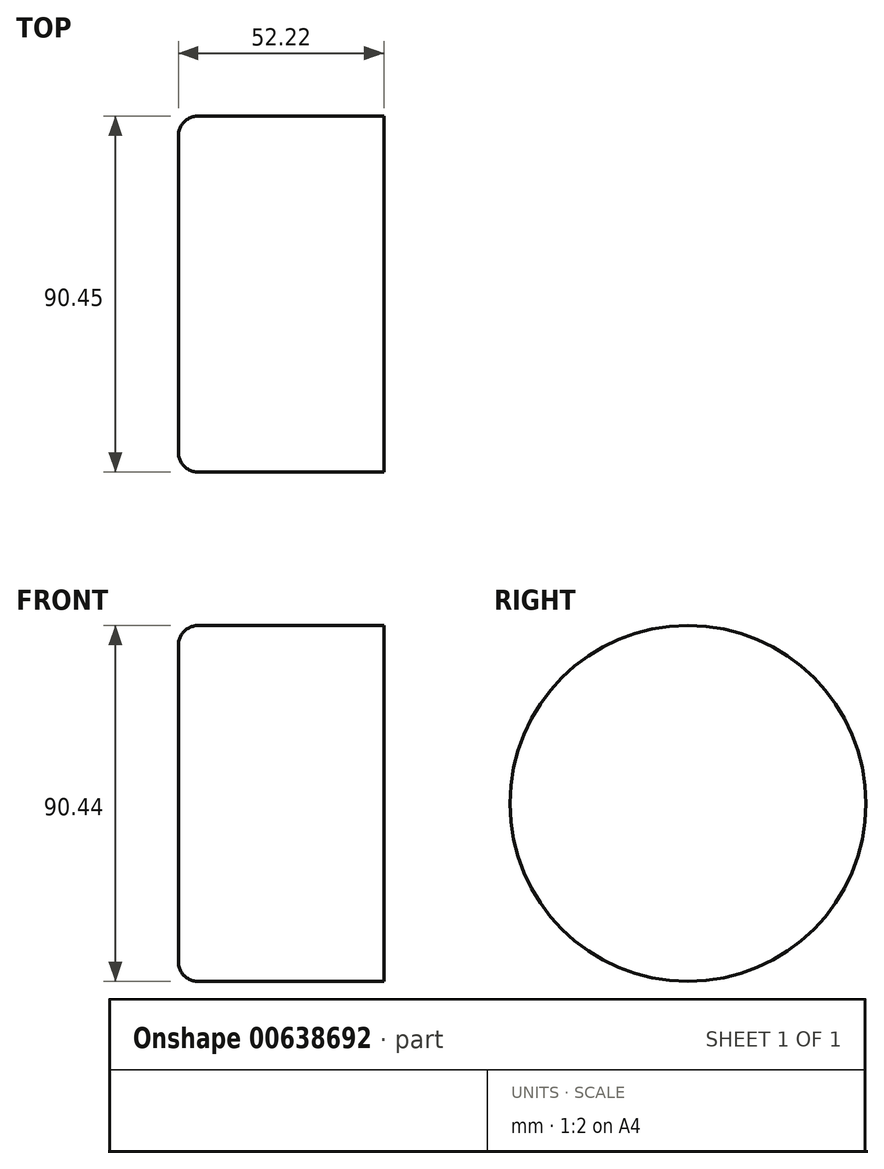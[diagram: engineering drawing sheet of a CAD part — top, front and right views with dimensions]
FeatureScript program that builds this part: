
annotation { "Feature Type Name" : "Feature", "Feature Type Description" : "" }
export const myFeature = defineFeature(function(context is Context, id is Id, definition is map)
    precondition{}
    {
        {
            var Q0;
            Q0=qCreatedBy(makeId("Right.planeOp"),FACE);
            var sketch = newSketch(context, id + "F0", { "sketchPlane" : qUnion([Q0])});
            skCircle(sketch, "E0", {"center": v(58.1, 0) * mm, "radius": 45.22 * mm});
            skSolve(sketch);
        }
        {
            var Q0;
            Q0=makeQuery(id+"F0.imprint","IMPRINT",FACE,{"disambiguationData":[TD([[makeQuery(id+"F0.imprint","IMPRINT",EDGE,{"derivedFrom":sQuery(id+"F0.wireOp",EDGE,"E0")}),1.0]])]});
            extrude(context, id + "F1", {"entities" : qUnion([Q0]), "depth" : 52.22 * mm, "offsetDistance" : 25.4 * mm});
        }
        {
            var Q0;
            Q0=makeQuery(id+"F1.opExtrude","CAP_EDGE",EDGE,{"disambiguationData":[OSD([sQuery(id+"F0.wireOp",EDGE,"E0")])],"isStart":true});
            fillet(context, id + "F2", {"entities" : qUnion([Q0]), "radius" : 5.08 * mm, "tangentPropagation" : true, "allowEdgeOverflow" : false});
        }
    });
